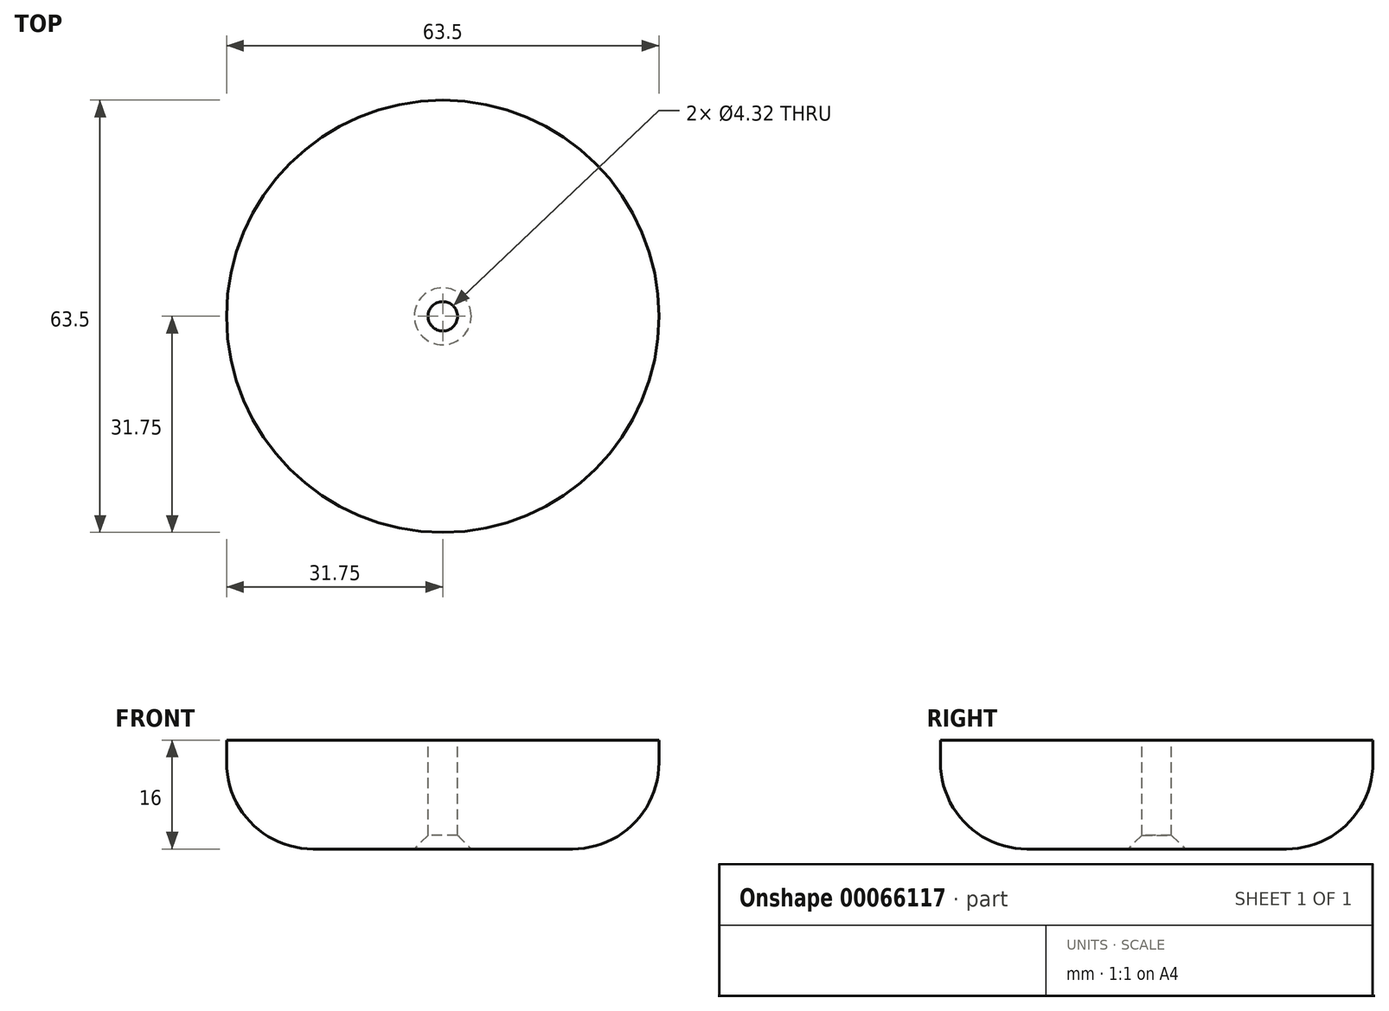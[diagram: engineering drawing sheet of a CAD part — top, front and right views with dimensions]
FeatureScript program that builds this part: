
annotation { "Feature Type Name" : "Feature", "Feature Type Description" : "" }
export const myFeature = defineFeature(function(context is Context, id is Id, definition is map)
    precondition{}
    {
        {
            var Q0;
            Q0=qCreatedBy(makeId("Top.planeOp"),FACE);
            var sketch = newSketch(context, id + "F0", { "sketchPlane" : qUnion([Q0])});
            skCircle(sketch, "E0", {"center": v(0, 0) * mm, "radius": 31.75 * mm});
            skSolve(sketch);
        }
        {
            var Q0;
            Q0 = qSketchRegion(id + "F0", true);
            extrude(context, id + "F1", {"entities" : qUnion([Q0]), "depth" : 16 * mm});
        }
        {
            var Q0;
            Q0=makeQuery(id+"F1.opExtrude","CAP_EDGE",EDGE,{"disambiguationData":[OSD([sQuery(id+"F0.wireOp",EDGE,"E0")])],"isStart":true});
            fillet(context, id + "F2", {"entities" : qUnion([Q0]), "radius" : 12.7 * mm, "tangentPropagation" : true, "allowEdgeOverflow" : false});
        }
        {
            var Q0;
            Q0=makeQuery(id+"F1.opExtrude","CAP_FACE",FACE,{"disambiguationData":[OSD([sQuery(id+"F0.wireOp",EDGE,"E0")])],"isStart":false});
            var sketch = newSketch(context, id + "F3", { "sketchPlane" : qUnion([Q0])});
            skCircle(sketch, "E1", {"center": v(0, 0) * mm, "radius": 2.16 * mm});
            skSolve(sketch);
        }
        {
            var Q0;
            Q0 = qSketchRegion(id + "F3", true);
            extrude(context, id + "F4", {"entities" : qUnion([Q0]), "operationType" : NewBodyOperationType.REMOVE, "endBound" : BoundingType.THROUGH_ALL, "oppositeDirection" : true, "depth" : 25.4 * mm});
        }
        {
            var Q0;
            Q0=makeQuery(id+"F4.boolean.opBoolean","INTERSECT",EDGE,{"derivedFrom":[makeQuery(id+"F1.opExtrude","CAP_FACE",FACE,{"disambiguationData":[OSD([sQuery(id+"F0.wireOp",EDGE,"E0")])],"isStart":true}),makeQuery(id+"F4.opExtrude","SWEPT_FACE",FACE,{"disambiguationData":[OSD([sQuery(id+"F3.wireOp",EDGE,"E1")])]})]});
            chamfer(context, id + "F5", {"entities" : qUnion([Q0]), "width" : 2.03 * mm, "tangentPropagation" : true});
        }
    });
